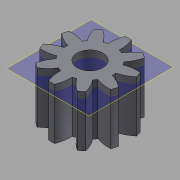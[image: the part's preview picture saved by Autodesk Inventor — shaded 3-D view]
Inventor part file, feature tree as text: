
AUTODESK INVENTOR PART (.ipt)
format: ipt  version: 2015 (Build 190159000, 159)  size: 167,424 bytes
history: native  units: in
note: dims shown in document units (in); Inventor stores cm internally (conversion verified against a paired STEP export)
features: other x13, sketch x3, plane x2
ambient origin geometry x8: Origin, YZ Plane, XZ Plane, XY Plane, X Axis, Y Axis, Z Axis, Center Point
bodies: Solid1 (feature_tree)
feature tree (18):
  other  "Spur Gear18_MIR3.ipt"
  other  "Solid1::Spur Gear18_MIR3.ipt"
  other  "TaggingFeature1"
  sketch  "Sketch1"  dims[d0=0.3937in]
  sketch  "Sketch2"  dims[d16=0.4528in d17=0.0in d41=0.0in d43=0.4528in d46=0.4528in d47=0.0in d48=0.0in]
  sketch  "Sketch3"
  plane  "XZ Plane_1"
  plane  "Work Plane2"
  other  "Z Axis_1"
  other  "Srf1"
  other  "Srf1::Derived"
  other  "Distance iMate"
  other  "Align iMate"
  other  "Mesh iMate"
  other  "Axis iMate"
  other  "Position iMate"
  other  "Mesh iMate2"
  other  "Start plane iMate"
